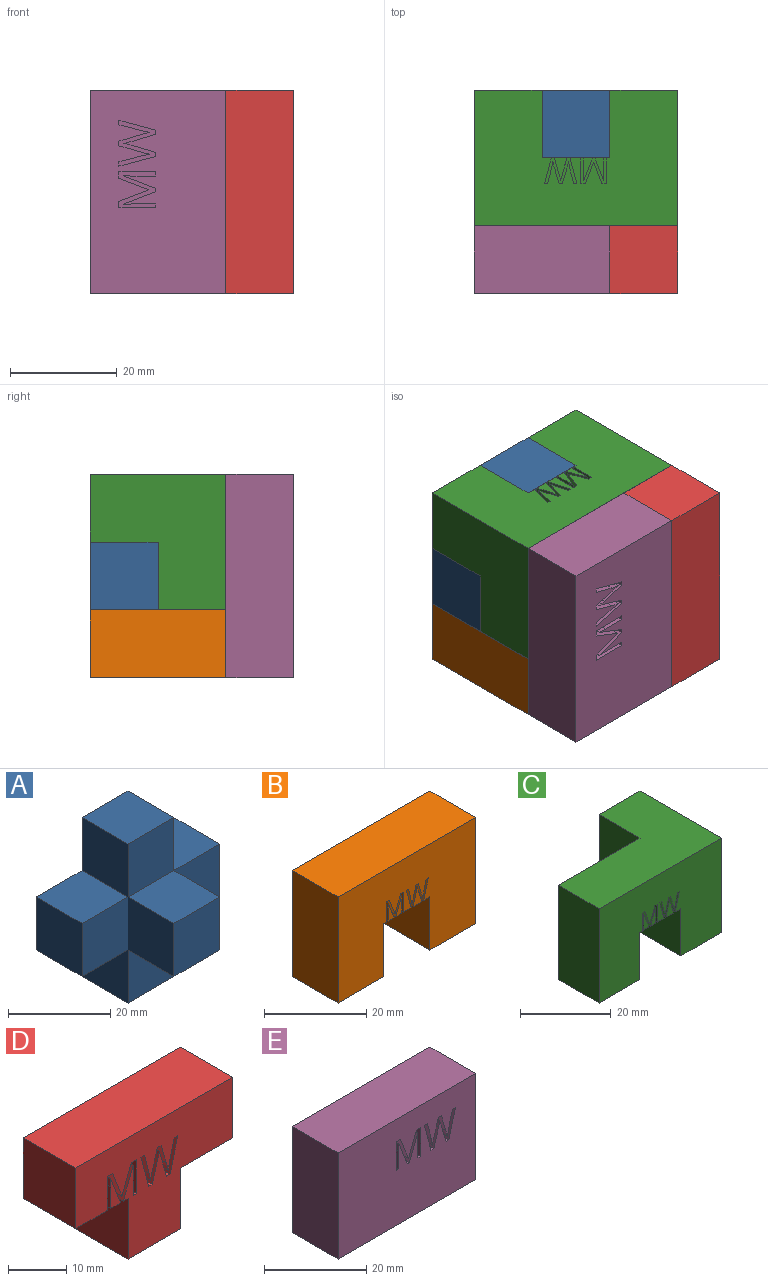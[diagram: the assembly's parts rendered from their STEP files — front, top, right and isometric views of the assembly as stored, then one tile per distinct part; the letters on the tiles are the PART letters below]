
ASSEMBLY  parts=5 mates=11
PART A: 62 faces, bbox 38.1x25.4x38.1 mm
  f0: plane 38.1x38.1mm, normal (0,1,0), area 786.6mm2, adj f4,f5,f6,f7,f8,f9,f10,f11
  f1: plane 12.7x12.7mm, normal (0,-1,0), area 161.3mm2, adj f10,f11,f12,f17
  f2: plane 12.7x12.7mm, normal (0,-1,0), area 161.3mm2, adj f7,f8,f9,f20
  f3: plane 12.7x12.7mm, normal (0,-1,0), area 161.3mm2, adj f4,f5,f6,f19
  f4: plane 12.7x12.7mm, normal (0,0,1), area 161.3mm2, adj f0,f3,f5,f15
  f5: plane 12.7x12.7mm, normal (-1,0,0), area 161.3mm2, adj f0,f3,f4,f6
  f6: plane 12.7x12.7mm, normal (0,0,-1), area 161.3mm2, adj f0,f3,f5,f7
  f7: plane 12.7x12.7mm, normal (-1,0,0), area 161.3mm2, adj f0,f2,f6,f8
  f8: plane 12.7x12.7mm, normal (0,0,-1), area 161.3mm2, adj f0,f2,f7,f9
  f9: plane 12.7x12.7mm, normal (1,0,0), area 161.3mm2, adj f0,f2,f8,f10
  f10: plane 12.7x12.7mm, normal (0,0,-1), area 161.3mm2, adj f0,f1,f9,f11
  f11: plane 12.7x12.7mm, normal (1,0,0), area 161.3mm2, adj f0,f1,f10,f12
  f12: plane 12.7x12.7mm, normal (0,0,1), area 161.3mm2, adj f0,f1,f11,f13
  f13: plane 12.7x12.7mm, normal (1,0,0), area 161.3mm2, adj f0,f12,f14,f16
  f14: plane 12.7x12.7mm, normal (0,0,1), area 161.3mm2, adj f0,f13,f15,f16
  f15: plane 12.7x12.7mm, normal (-1,0,0), area 161.3mm2, adj f0,f4,f14,f16
  f16: plane 12.7x12.7mm, normal (0,-1,0), area 161.3mm2, adj f13,f14,f15,f18
  f17: plane 12.7x12.7mm, normal (1,0,0), area 161.3mm2, adj f1,f18,f20,f21
  f18: plane 12.7x12.7mm, normal (0,0,1), area 161.3mm2, adj f16,f17,f19,f21
  f19: plane 12.7x12.7mm, normal (-1,0,0), area 161.3mm2, adj f3,f18,f20,f21
  f20: plane 12.7x12.7mm, normal (0,0,-1), area 161.3mm2, adj f2,f17,f19,f21
  f21: plane 12.7x12.7mm, normal (0,-1,0), area 161.3mm2, adj f17,f18,f19,f20
  f22: plane 2.54x0.55mm, normal (0,0,1), area 1.4mm2, adj f0,f23,f41,f42
  f23: plane 4.82x2.54mm, normal (0.97,0,0.26), area 12.7mm2, adj f0,f22,f24,f42
  f24: plane 2.54x0.59mm, normal (0,0,-1), area 1.5mm2, adj f0,f23,f25,f42
  f25: plane 2.97x2.54mm, normal (-0.97,0,-0.25), area 7.8mm2, adj f0,f24,f26,f42
  f26: extruded ~2.54x1.14mm, area 3mm2, adj f0,f25,f27,f42
  f27: extruded ~2.54x1.16mm, area 3mm2, adj f0,f26,f28,f42
  f28: plane 2.96x2.54mm, normal (0.96,0,-0.29), area 7.9mm2, adj f0,f27,f29,f42
  f29: plane 2.54x0.59mm, normal (0,0,-1), area 1.5mm2, adj f0,f28,f30,f42
  f30: plane 2.93x2.54mm, normal (-0.96,0,-0.28), area 7.8mm2, adj f0,f29,f31,f42
  f31: extruded ~2.54x1.18mm, area 3.1mm2, adj f0,f30,f32,f42
  f32: extruded ~2.54x1.13mm, area 2.9mm2, adj f0,f31,f33,f42
  f33: plane 2.98x2.54mm, normal (0.97,0,-0.25), area 7.8mm2, adj f0,f32,f34,f42
  f34: plane 2.54x0.59mm, normal (0,0,-1), area 1.5mm2, adj f0,f33,f35,f42
  f35: plane 4.82x2.54mm, normal (-0.97,0,0.26), area 12.7mm2, adj f0,f34,f36,f42
  f36: plane 2.54x0.55mm, normal (0,0,1), area 1.4mm2, adj f0,f35,f37,f42
  f37: plane 3.21x2.54mm, normal (0.96,0,0.28), area 8.5mm2, adj f0,f36,f38,f42
  f38: extruded ~2.54x0.95mm, area 2.5mm2, adj f0,f37,f39,f42
  f39: extruded ~2.54x0.39mm, area 1mm2, adj f0,f38,f40,f42
  f40: extruded ~2.54x0.54mm, area 1.4mm2, adj f0,f39,f41,f42
  f41: plane 3.23x2.54mm, normal (-0.96,0,0.29), area 8.6mm2, adj f0,f22,f40,f42
  f42: plane 6.07x4.82mm, normal (0,1,0), area 9.9mm2, adj f22,f23,f24,f25,f26,f27,f28,f29
  f43: plane 4.28x2.54mm, normal (-0.93,0,0.36), area 11.6mm2, adj f0,f44,f60,f61
  f44: plane 2.54x0.45mm, normal (0,0,1), area 1.1mm2, adj f0,f43,f45,f61
  f45: plane 4.27x2.54mm, normal (0.93,0,0.36), area 11.6mm2, adj f0,f44,f46,f61
  f46: plane 2.54x0.03mm, normal (0,0,1), area 0.1mm2, adj f0,f45,f47,f61
  f47: extruded ~2.54x1.16mm, area 3mm2, adj f0,f46,f48,f61
  f48: plane 3.11x2.54mm, normal (-1,0,0), area 7.9mm2, adj f0,f47,f49,f61
  f49: plane 2.54x0.56mm, normal (0,0,1), area 1.4mm2, adj f0,f48,f50,f61
  f50: plane 4.82x2.54mm, normal (1,0,0), area 12.3mm2, adj f0,f49,f51,f61
  f51: plane 2.54x0.84mm, normal (0,0,-1), area 2.1mm2, adj f0,f50,f52,f61
  f52: plane 3.98x2.54mm, normal (-0.93,0,-0.36), area 10.8mm2, adj f0,f51,f53,f61
  f53: plane 2.54x0.03mm, normal (0,0,-1), area 0.1mm2, adj f0,f52,f54,f61
  f54: plane 3.98x2.54mm, normal (0.93,0,-0.36), area 10.8mm2, adj f0,f53,f55,f61
  f55: plane 2.54x0.84mm, normal (0,0,-1), area 2.1mm2, adj f0,f54,f56,f61
  f56: plane 4.82x2.54mm, normal (-1,0,0), area 12.3mm2, adj f0,f55,f57,f61
  f57: plane 2.54x0.52mm, normal (0,0,1), area 1.3mm2, adj f0,f56,f58,f61
  f58: plane 3.07x2.54mm, normal (1,0,0), area 7.8mm2, adj f0,f57,f59,f61
  f59: extruded ~2.54x1.21mm, area 3.1mm2, adj f0,f58,f60,f61
  f60: plane 2.54x0.03mm, normal (0,0,1), area 0.1mm2, adj f0,f43,f59,f61
  f61: plane 4.82x4.78mm, normal (0,1,0), area 9.9mm2, adj f43,f44,f45,f46,f47,f48,f49,f50
PART B: 48 faces, bbox 38.1x12.7x25.4 mm
  f0: plane 12.7x12.7mm, normal (0,0,-1), area 154.6mm2, adj f1,f2,f3,f4,f5,f11,f12,f13
  f1: plane 4.16x2.39mm, normal (0,-1,0), area 4.8mm2, adj f0,f29,f43,f44,f45,f46
  f2: plane 38.1x25.4mm, normal (0,-1,0), area 774.9mm2, adj f0,f5,f6,f7,f8,f9,f10,f11
  f3: plane 4.28x1.66mm, normal (0,-1,0), area 3.4mm2, adj f0,f13,f25,f26,f27
  f4: plane 4.27x1.68mm, normal (0,-1,0), area 3.5mm2, adj f0,f14,f15,f16,f17
  f5: plane 12.7x12.7mm, normal (-1,0,0), area 161.3mm2, adj f0,f2,f6,f12
  f6: plane 12.7x12.7mm, normal (0,0,-1), area 161.3mm2, adj f2,f5,f7,f12
  f7: plane 25.4x12.7mm, normal (1,0,0), area 322.6mm2, adj f2,f6,f8,f12
  f8: plane 38.1x12.7mm, normal (0,0,1), area 483.9mm2, adj f2,f7,f9,f12
  f9: plane 25.4x12.7mm, normal (-1,0,0), area 322.6mm2, adj f2,f8,f10,f12
  f10: plane 12.7x12.7mm, normal (0,0,-1), area 161.3mm2, adj f2,f9,f11,f12
  f11: plane 12.7x12.7mm, normal (1,0,0), area 161.3mm2, adj f0,f2,f10,f12
  f12: plane 38.1x25.4mm, normal (0,1,0), area 806.4mm2, adj f0,f5,f6,f7,f8,f9,f10,f11
  f13: plane 4.28x2.54mm, normal (0.93,0,0.36), area 11.6mm2, adj f0,f3,f27,f28
  f14: plane 4.27x2.54mm, normal (-0.93,0,0.36), area 11.6mm2, adj f0,f4,f15,f28
  f15: plane 2.54x0.03mm, normal (0,0,1), area 0.1mm2, adj f4,f14,f16,f28
  f16: extruded ~2.54x1.16mm, area 3mm2, adj f4,f15,f17,f28
  f17: plane 3.11x2.54mm, normal (1,0,0), area 7.9mm2, adj f0,f4,f16,f28
  f18: plane 4.82x2.54mm, normal (-1,0,0), area 12.3mm2, adj f0,f2,f19,f28
  f19: plane 2.54x0.84mm, normal (0,0,-1), area 2.1mm2, adj f2,f18,f20,f28
  f20: plane 3.98x2.54mm, normal (0.93,0,-0.36), area 10.8mm2, adj f2,f19,f21,f28
  f21: plane 2.54x0.03mm, normal (0,0,-1), area 0.1mm2, adj f2,f20,f22,f28
  f22: plane 3.98x2.54mm, normal (-0.93,0,-0.36), area 10.8mm2, adj f2,f21,f23,f28
  f23: plane 2.54x0.84mm, normal (0,0,-1), area 2.1mm2, adj f2,f22,f24,f28
  f24: plane 4.82x2.54mm, normal (1,0,0), area 12.3mm2, adj f0,f2,f23,f28
  f25: plane 3.07x2.54mm, normal (-1,0,0), area 7.8mm2, adj f0,f3,f26,f28
  f26: extruded ~2.54x1.21mm, area 3.1mm2, adj f3,f25,f27,f28
  f27: plane 2.54x0.03mm, normal (0,0,1), area 0.1mm2, adj f3,f13,f26,f28
  f28: plane 4.82x4.78mm, normal (0,-1,0), area 9.9mm2, adj f0,f13,f14,f15,f16,f17,f18,f19
  f29: plane 3.23x2.54mm, normal (0.96,0,0.29), area 8.6mm2, adj f0,f1,f46,f47
  f30: plane 4.82x2.54mm, normal (-0.97,0,0.26), area 12.7mm2, adj f0,f2,f31,f47
  f31: plane 2.54x0.59mm, normal (0,0,-1), area 1.5mm2, adj f2,f30,f32,f47
  f32: plane 2.97x2.54mm, normal (0.97,0,-0.25), area 7.8mm2, adj f2,f31,f33,f47
  f33: extruded ~2.54x1.14mm, area 3mm2, adj f2,f32,f34,f47
  f34: extruded ~2.54x1.16mm, area 3mm2, adj f2,f33,f35,f47
  f35: plane 2.96x2.54mm, normal (-0.96,0,-0.29), area 7.9mm2, adj f2,f34,f36,f47
  f36: plane 2.54x0.59mm, normal (0,0,-1), area 1.5mm2, adj f2,f35,f37,f47
  f37: plane 2.93x2.54mm, normal (0.96,0,-0.28), area 7.8mm2, adj f2,f36,f38,f47
  f38: extruded ~2.54x1.18mm, area 3.1mm2, adj f2,f37,f39,f47
  f39: extruded ~2.54x1.13mm, area 2.9mm2, adj f2,f38,f40,f47
  f40: plane 2.98x2.54mm, normal (-0.97,0,-0.25), area 7.8mm2, adj f2,f39,f41,f47
  f41: plane 2.54x0.59mm, normal (0,0,-1), area 1.5mm2, adj f2,f40,f42,f47
  f42: plane 4.82x2.54mm, normal (0.97,0,0.26), area 12.7mm2, adj f0,f2,f41,f47
  f43: plane 3.21x2.54mm, normal (-0.96,0,0.28), area 8.5mm2, adj f0,f1,f44,f47
  f44: extruded ~2.54x0.95mm, area 2.5mm2, adj f1,f43,f45,f47
  f45: extruded ~2.54x0.39mm, area 1mm2, adj f1,f44,f46,f47
  f46: extruded ~2.54x0.54mm, area 1.4mm2, adj f1,f29,f45,f47
  f47: plane 6.07x4.82mm, normal (0,-1,0), area 9.9mm2, adj f0,f29,f30,f31,f32,f33,f34,f35
PART C: 52 faces, bbox 38.1x25.4x25.4 mm
  f0: plane 12.7x12.7mm, normal (0,1,0), area 161.3mm2, adj f6,f7,f8,f49
  f1: plane 12.7x12.7mm, normal (0,0,-1), area 154.6mm2, adj f2,f3,f4,f5,f6,f12,f13,f14
  f2: plane 4.16x2.39mm, normal (0,-1,0), area 4.8mm2, adj f1,f30,f44,f45,f46,f47
  f3: plane 38.1x25.4mm, normal (0,-1,0), area 774.9mm2, adj f1,f6,f7,f8,f9,f10,f11,f12
  f4: plane 4.28x1.66mm, normal (0,-1,0), area 3.4mm2, adj f1,f14,f26,f27,f28
  f5: plane 4.27x1.68mm, normal (0,-1,0), area 3.5mm2, adj f1,f15,f16,f17,f18
  f6: plane 12.7x12.7mm, normal (-1,0,0), area 161.3mm2, adj f0,f1,f3,f7
  f7: plane 12.7x12.7mm, normal (0,0,-1), area 161.3mm2, adj f0,f3,f6,f8
  f8: plane 25.4x25.4mm, normal (1,0,0), area 483.9mm2, adj f0,f3,f7,f9,f49,f51
  f9: plane 38.1x25.4mm, normal (0,0,1), area 645.2mm2, adj f3,f8,f10,f13,f50,f51
  f10: plane 25.4x12.7mm, normal (-1,0,0), area 322.6mm2, adj f3,f9,f11,f13
  f11: plane 12.7x12.7mm, normal (0,0,-1), area 161.3mm2, adj f3,f10,f12,f13
  f12: plane 12.7x12.7mm, normal (1,0,0), area 161.3mm2, adj f1,f3,f11,f13
  f13: plane 25.4x25.4mm, normal (0,1,0), area 483.9mm2, adj f1,f9,f10,f11,f12,f50
  f14: plane 4.28x2.54mm, normal (0.93,0,0.36), area 11.6mm2, adj f1,f4,f28,f29
  f15: plane 4.27x2.54mm, normal (-0.93,0,0.36), area 11.6mm2, adj f1,f5,f16,f29
  f16: plane 2.54x0.03mm, normal (0,0,1), area 0.1mm2, adj f5,f15,f17,f29
  f17: extruded ~2.54x1.16mm, area 3mm2, adj f5,f16,f18,f29
  f18: plane 3.11x2.54mm, normal (1,0,0), area 7.9mm2, adj f1,f5,f17,f29
  f19: plane 4.82x2.54mm, normal (-1,0,0), area 12.3mm2, adj f1,f3,f20,f29
  f20: plane 2.54x0.84mm, normal (0,0,-1), area 2.1mm2, adj f3,f19,f21,f29
  f21: plane 3.98x2.54mm, normal (0.93,0,-0.36), area 10.8mm2, adj f3,f20,f22,f29
  f22: plane 2.54x0.03mm, normal (0,0,-1), area 0.1mm2, adj f3,f21,f23,f29
  f23: plane 3.98x2.54mm, normal (-0.93,0,-0.36), area 10.8mm2, adj f3,f22,f24,f29
  f24: plane 2.54x0.84mm, normal (0,0,-1), area 2.1mm2, adj f3,f23,f25,f29
  f25: plane 4.82x2.54mm, normal (1,0,0), area 12.3mm2, adj f1,f3,f24,f29
  f26: plane 3.07x2.54mm, normal (-1,0,0), area 7.8mm2, adj f1,f4,f27,f29
  f27: extruded ~2.54x1.21mm, area 3.1mm2, adj f4,f26,f28,f29
  f28: plane 2.54x0.03mm, normal (0,0,1), area 0.1mm2, adj f4,f14,f27,f29
  f29: plane 4.82x4.78mm, normal (0,-1,0), area 9.9mm2, adj f1,f14,f15,f16,f17,f18,f19,f20
  f30: plane 3.23x2.54mm, normal (0.96,0,0.29), area 8.6mm2, adj f1,f2,f47,f48
  f31: plane 4.82x2.54mm, normal (-0.97,0,0.26), area 12.7mm2, adj f1,f3,f32,f48
  f32: plane 2.54x0.59mm, normal (0,0,-1), area 1.5mm2, adj f3,f31,f33,f48
  f33: plane 2.97x2.54mm, normal (0.97,0,-0.25), area 7.8mm2, adj f3,f32,f34,f48
  f34: extruded ~2.54x1.14mm, area 3mm2, adj f3,f33,f35,f48
  f35: extruded ~2.54x1.16mm, area 3mm2, adj f3,f34,f36,f48
  f36: plane 2.96x2.54mm, normal (-0.96,0,-0.29), area 7.9mm2, adj f3,f35,f37,f48
  f37: plane 2.54x0.59mm, normal (0,0,-1), area 1.5mm2, adj f3,f36,f38,f48
  f38: plane 2.93x2.54mm, normal (0.96,0,-0.28), area 7.8mm2, adj f3,f37,f39,f48
  f39: extruded ~2.54x1.18mm, area 3.1mm2, adj f3,f38,f40,f48
  f40: extruded ~2.54x1.13mm, area 2.9mm2, adj f3,f39,f41,f48
  f41: plane 2.98x2.54mm, normal (-0.97,0,-0.25), area 7.8mm2, adj f3,f40,f42,f48
  f42: plane 2.54x0.59mm, normal (0,0,-1), area 1.5mm2, adj f3,f41,f43,f48
  f43: plane 4.82x2.54mm, normal (0.97,0,0.26), area 12.7mm2, adj f1,f3,f42,f48
  f44: plane 3.21x2.54mm, normal (-0.96,0,0.28), area 8.5mm2, adj f1,f2,f45,f48
  f45: extruded ~2.54x0.95mm, area 2.5mm2, adj f2,f44,f46,f48
  f46: extruded ~2.54x0.39mm, area 1mm2, adj f2,f45,f47,f48
  f47: extruded ~2.54x0.54mm, area 1.4mm2, adj f2,f30,f46,f48
  f48: plane 6.07x4.82mm, normal (0,-1,0), area 9.9mm2, adj f1,f30,f31,f32,f33,f34,f35,f36
  f49: plane 12.7x12.7mm, normal (0,0,-1), area 161.3mm2, adj f0,f8,f50,f51
  f50: plane 12.7x12.7mm, normal (-1,0,0), area 161.3mm2, adj f9,f13,f49,f51
  f51: plane 12.7x12.7mm, normal (0,1,0), area 161.3mm2, adj f8,f9,f49,f50
PART D: 49 faces, bbox 38.1x12.7x25.4 mm
  f0: plane 12.7x12.7mm, normal (0,0,-1), area 157.7mm2, adj f1,f2,f3,f9,f10,f11,f12,f23
  f1: plane 6.28x2.44mm, normal (0,-1,0), area 7.4mm2, adj f0,f11,f24,f25,f26
  f2: plane 38.1x25.4mm, normal (0,-1,0), area 595mm2, adj f0,f3,f4,f5,f6,f7,f8,f9
  f3: plane 12.7x12.7mm, normal (-1,0,0), area 161.3mm2, adj f0,f2,f4,f10
  f4: plane 12.7x12.7mm, normal (0,0,-1), area 161.3mm2, adj f2,f3,f5,f10
  f5: plane 12.7x12.7mm, normal (1,0,0), area 161.3mm2, adj f2,f4,f6,f10
  f6: plane 12.7x12.7mm, normal (0,0,-1), area 161.3mm2, adj f2,f5,f7,f10
  f7: plane 12.7x12.7mm, normal (1,0,0), area 161.3mm2, adj f2,f6,f8,f10
  f8: plane 38.1x12.7mm, normal (0,0,1), area 483.9mm2, adj f2,f7,f9,f10
  f9: plane 12.7x12.7mm, normal (-1,0,0), area 161.3mm2, adj f0,f2,f8,f10
  f10: plane 38.1x25.4mm, normal (0,1,0), area 645.2mm2, adj f0,f3,f4,f5,f6,f7,f8,f9
  f11: plane 6.28x2.54mm, normal (0.93,0,0.36), area 17.1mm2, adj f0,f1,f26,f27
  f12: plane 6.27x2.54mm, normal (-0.93,0,0.36), area 17.1mm2, adj f0,f2,f13,f27
  f13: plane 2.54x0.04mm, normal (0,0,1), area 0.1mm2, adj f2,f12,f14,f27
  f14: extruded ~2.54x1.7mm, area 4.3mm2, adj f2,f13,f15,f27
  f15: plane 4.56x2.54mm, normal (1,0,0), area 11.6mm2, adj f2,f14,f16,f27
  f16: plane 2.54x0.82mm, normal (0,0,1), area 2.1mm2, adj f2,f15,f17,f27
  f17: plane 7.08x2.54mm, normal (-1,0,0), area 18mm2, adj f2,f16,f18,f27
  f18: plane 2.54x1.23mm, normal (0,0,-1), area 3.1mm2, adj f2,f17,f19,f27
  f19: plane 5.84x2.54mm, normal (0.93,0,-0.36), area 15.9mm2, adj f2,f18,f20,f27
  f20: plane 2.54x0.04mm, normal (0,0,-1), area 0.1mm2, adj f2,f19,f21,f27
  f21: plane 5.84x2.54mm, normal (-0.93,0,-0.36), area 15.9mm2, adj f2,f20,f22,f27
  f22: plane 2.54x1.24mm, normal (0,0,-1), area 3.1mm2, adj f2,f21,f23,f27
  f23: plane 7.08x2.54mm, normal (1,0,0), area 18mm2, adj f0,f2,f22,f27
  f24: plane 4.5x2.54mm, normal (-1,0,0), area 11.4mm2, adj f0,f1,f25,f27
  f25: extruded ~2.54x1.77mm, area 4.5mm2, adj f1,f24,f26,f27
  f26: plane 2.54x0.04mm, normal (0,0,1), area 0.1mm2, adj f1,f11,f25,f27
  f27: plane 7.08x7.01mm, normal (0,-1,0), area 21.4mm2, adj f0,f11,f12,f13,f14,f15,f16,f17
  f28: plane 2.54x0.81mm, normal (0,0,1), area 2.1mm2, adj f2,f29,f47,f48
  f29: plane 7.08x2.54mm, normal (-0.97,0,0.26), area 18.6mm2, adj f2,f28,f30,f48
  f30: plane 2.54x0.87mm, normal (0,0,-1), area 2.2mm2, adj f2,f29,f31,f48
  f31: plane 4.36x2.54mm, normal (0.97,0,-0.25), area 11.4mm2, adj f2,f30,f32,f48
  f32: extruded ~2.54x1.68mm, area 4.3mm2, adj f2,f31,f33,f48
  f33: extruded ~2.54x1.7mm, area 4.4mm2, adj f2,f32,f34,f48
  f34: plane 4.34x2.54mm, normal (-0.96,0,-0.29), area 11.5mm2, adj f2,f33,f35,f48
  f35: plane 2.54x0.87mm, normal (0,0,-1), area 2.2mm2, adj f2,f34,f36,f48
  f36: plane 4.3x2.54mm, normal (0.96,0,-0.28), area 11.4mm2, adj f2,f35,f37,f48
  f37: extruded ~2.54x1.73mm, area 4.5mm2, adj f2,f36,f38,f48
  f38: extruded ~2.54x1.67mm, area 4.3mm2, adj f2,f37,f39,f48
  f39: plane 4.37x2.54mm, normal (-0.97,0,-0.25), area 11.5mm2, adj f2,f38,f40,f48
  f40: plane 2.54x0.87mm, normal (0,0,-1), area 2.2mm2, adj f2,f39,f41,f48
  f41: plane 7.08x2.54mm, normal (0.97,0,0.26), area 18.6mm2, adj f2,f40,f42,f48
  f42: plane 2.54x0.81mm, normal (0,0,1), area 2.1mm2, adj f2,f41,f43,f48
  f43: plane 4.71x2.54mm, normal (-0.96,0,0.28), area 12.5mm2, adj f2,f42,f44,f48
  f44: extruded ~2.54x1.4mm, area 3.7mm2, adj f2,f43,f45,f48
  f45: extruded ~2.54x0.58mm, area 1.5mm2, adj f2,f44,f46,f48
  f46: extruded ~2.54x0.8mm, area 2.1mm2, adj f2,f45,f47,f48
  f47: plane 4.74x2.54mm, normal (0.96,0,0.29), area 12.6mm2, adj f2,f28,f46,f48
  f48: plane 8.92x7.08mm, normal (0,-1,0), area 21.4mm2, adj f28,f29,f30,f31,f32,f33,f34,f35
PART E: 46 faces, bbox 38.1x12.7x25.4 mm
  f0: plane 38.1x25.4mm, normal (0,-1,0), area 928mm2, adj f1,f2,f3,f4,f6,f7,f8,f9
  f1: plane 38.1x12.7mm, normal (0,0,1), area 483.9mm2, adj f0,f2,f4,f5
  f2: plane 25.4x12.7mm, normal (-1,0,0), area 322.6mm2, adj f0,f1,f3,f5
  f3: plane 38.1x12.7mm, normal (0,0,-1), area 483.9mm2, adj f0,f2,f4,f5
  f4: plane 25.4x12.7mm, normal (1,0,0), area 322.6mm2, adj f0,f1,f3,f5
  f5: plane 38.1x25.4mm, normal (0,1,0), area 967.7mm2, adj f1,f2,f3,f4
  f6: plane 2.54x0.78mm, normal (0,0,1), area 2mm2, adj f0,f7,f25,f26
  f7: plane 6.82x2.54mm, normal (-0.97,0,0.26), area 17.9mm2, adj f0,f6,f8,f26
  f8: plane 2.54x0.84mm, normal (0,0,-1), area 2.1mm2, adj f0,f7,f9,f26
  f9: plane 4.2x2.54mm, normal (0.97,0,-0.25), area 11mm2, adj f0,f8,f10,f26
  f10: extruded ~2.54x1.61mm, area 4.2mm2, adj f0,f9,f11,f26
  f11: extruded ~2.54x1.63mm, area 4.3mm2, adj f0,f10,f12,f26
  f12: plane 4.18x2.54mm, normal (-0.96,0,-0.29), area 11.1mm2, adj f0,f11,f13,f26
  f13: plane 2.54x0.84mm, normal (0,0,-1), area 2.1mm2, adj f0,f12,f14,f26
  f14: plane 4.15x2.54mm, normal (0.96,0,-0.28), area 11mm2, adj f0,f13,f15,f26
  f15: extruded ~2.54x1.67mm, area 4.3mm2, adj f0,f14,f16,f26
  f16: extruded ~2.54x1.6mm, area 4.2mm2, adj f0,f15,f17,f26
  f17: plane 4.21x2.54mm, normal (-0.97,0,-0.25), area 11mm2, adj f0,f16,f18,f26
  f18: plane 2.54x0.84mm, normal (0,0,-1), area 2.1mm2, adj f0,f17,f19,f26
  f19: plane 6.82x2.54mm, normal (0.97,0,0.26), area 17.9mm2, adj f0,f18,f20,f26
  f20: plane 2.54x0.78mm, normal (0,0,1), area 2mm2, adj f0,f19,f21,f26
  f21: plane 4.54x2.54mm, normal (-0.96,0,0.28), area 12mm2, adj f0,f20,f22,f26
  f22: extruded ~2.54x1.35mm, area 3.5mm2, adj f0,f21,f23,f26
  f23: extruded ~2.54x0.56mm, area 1.4mm2, adj f0,f22,f24,f26
  f24: extruded ~2.54x0.77mm, area 2mm2, adj f0,f23,f25,f26
  f25: plane 4.56x2.54mm, normal (0.96,0,0.29), area 12.1mm2, adj f0,f6,f24,f26
  f26: plane 8.59x6.82mm, normal (0,-1,0), area 19.8mm2, adj f6,f7,f8,f9,f10,f11,f12,f13
  f27: plane 6.04x2.54mm, normal (0.93,0,0.36), area 16.4mm2, adj f0,f28,f44,f45
  f28: plane 2.54x0.64mm, normal (0,0,1), area 1.6mm2, adj f0,f27,f29,f45
  f29: plane 6.03x2.54mm, normal (-0.93,0,0.36), area 16.4mm2, adj f0,f28,f30,f45
  f30: plane 2.54x0.04mm, normal (0,0,1), area 0.1mm2, adj f0,f29,f31,f45
  f31: extruded ~2.54x1.64mm, area 4.2mm2, adj f0,f30,f32,f45
  f32: plane 4.39x2.54mm, normal (1,0,0), area 11.2mm2, adj f0,f31,f33,f45
  f33: plane 2.54x0.79mm, normal (0,0,1), area 2mm2, adj f0,f32,f34,f45
  f34: plane 6.82x2.54mm, normal (-1,0,0), area 17.3mm2, adj f0,f33,f35,f45
  f35: plane 2.54x1.18mm, normal (0,0,-1), area 3mm2, adj f0,f34,f36,f45
  f36: plane 5.62x2.54mm, normal (0.93,0,-0.36), area 15.3mm2, adj f0,f35,f37,f45
  f37: plane 2.54x0.04mm, normal (0,0,-1), area 0.1mm2, adj f0,f36,f38,f45
  f38: plane 5.62x2.54mm, normal (-0.93,0,-0.36), area 15.3mm2, adj f0,f37,f39,f45
  f39: plane 2.54x1.19mm, normal (0,0,-1), area 3mm2, adj f0,f38,f40,f45
  f40: plane 6.82x2.54mm, normal (1,0,0), area 17.3mm2, adj f0,f39,f41,f45
  f41: plane 2.54x0.73mm, normal (0,0,1), area 1.9mm2, adj f0,f40,f42,f45
  f42: plane 4.34x2.54mm, normal (-1,0,0), area 11mm2, adj f0,f41,f43,f45
  f43: extruded ~2.54x1.71mm, area 4.3mm2, adj f0,f42,f44,f45
  f44: plane 2.54x0.04mm, normal (0,0,1), area 0.1mm2, adj f0,f27,f43,f45
  f45: plane 6.82x6.75mm, normal (0,-1,0), area 19.9mm2, adj f27,f28,f29,f30,f31,f32,f33,f34
PLACE A at identity fixed
PLACE B rot(axis=(1,0,0),90deg) t=(7.21,2.46,-6.35)mm
PLACE C rot(axis=(0,-0.71,0.71),180deg) t=(-7.21,2.46,6.35)mm
PLACE D rot(axis=(0.58,-0.58,0.58),120deg) t=(6.35,-25.4,0)mm
PLACE E rot(axis=(0,-1,0),90deg) t=(-2.36,-25.4,3.15)mm fixed
MATE planar D.f3 <-> B.f12  axis (0,0,-1) through (12.7,-12.7,-6.35)mm
MATE planar A.f17 <-> D.f10  axis (1,0,0) through (6.35,-19.05,0)mm
MATE planar C.f1 <-> A.f16  axis (0,1,0) through (-0.03,-12.7,12.48)mm
MATE planar C.f13 <-> A.f18  axis (0,0,-1) through (8.47,-14.82,6.35)mm
MATE planar D.f4 <-> A.f1  axis (0,1,0) through (12.7,-12.7,0)mm
MATE planar A.f1 <-> D.f4  axis (0,-1,0) through (12.7,-12.7,0)mm
MATE planar A.f2 <-> B.f0  axis (0,-1,0) through (0,-12.7,-12.7)mm
MATE parallel A.f20 <-> B.f12  axis (0,0,-1) through (0,-19.05,-6.35)mm
MATE planar E.f5 <-> A.f21  axis (0,1,0) through (-6.35,-25.4,0)mm
MATE planar D.f10 <-> E.f3  axis (-1,0,0) through (6.35,-28.58,0)mm
MATE planar C.f6 <-> A.f15  axis (1,0,0) through (-6.35,-6.35,12.7)mm
